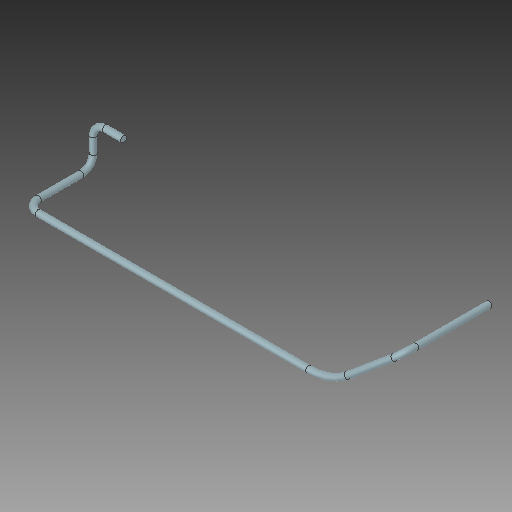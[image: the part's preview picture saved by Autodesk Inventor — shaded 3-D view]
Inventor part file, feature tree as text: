
AUTODESK INVENTOR PART (.ipt)
format: ipt  version: 2019 (Build 230136000, 136)  size: 108,032 bytes
history: native  units: in
note: dims shown in document units (in); Inventor stores cm internally (conversion verified against a paired STEP export)
features: sketch x4, plane x4, other x3
ambient origin geometry x8: Origin, YZ Plane, XZ Plane, XY Plane, X Axis, Y Axis, Z Axis, Center Point
bodies: Solid1 (feature_tree)
feature tree (11):
  other  "Side Mounting Bar.ipt"
  other  "Solid1::Side Mounting Bar.ipt"
  other  "TaggingFeature1"
  sketch  "Sketch2"  dims[d0=0.3937in]
  sketch  "Sketch3"
  sketch  "Sketch4"
  sketch  "Sketch5"
  plane  "Work Plane1"
  plane  "Work Plane2"
  plane  "Work Plane3"
  plane  "Work Plane4"
